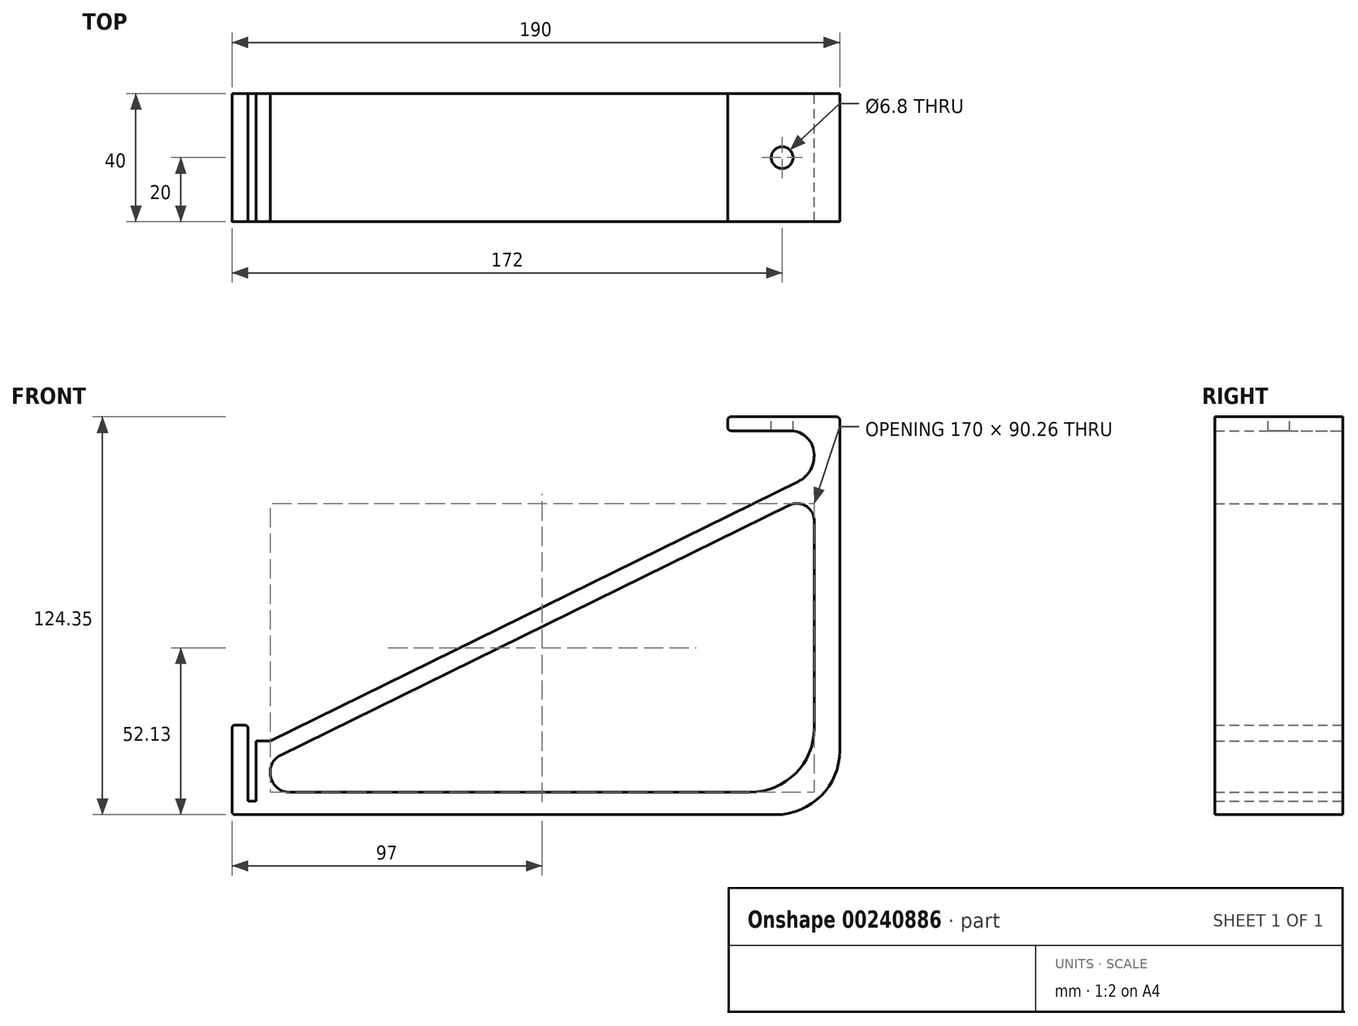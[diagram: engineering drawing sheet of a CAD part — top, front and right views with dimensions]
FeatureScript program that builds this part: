
annotation { "Feature Type Name" : "Feature", "Feature Type Description" : "" }
export const myFeature = defineFeature(function(context is Context, id is Id, definition is map)
    precondition{}
    {
        {
            var Q0;
            Q0=qCreatedBy(makeId("Front.planeOp"),FACE);
            var sketch = newSketch(context, id + "F0", { "sketchPlane" : qUnion([Q0])});
            skLineSegment(sketch, "E0", {"start": v(182, 27) * mm, "end": v(182, 91.87) * mm});
            skLineSegment(sketch, "E1", {"start": v(174.5, 120) * mm, "end": v(156, 120) * mm});
            skLineSegment(sketch, "E2", {"start": v(155, 121) * mm, "end": v(155, 123.35) * mm});
            skLineSegment(sketch, "E3", {"start": v(156, 124.35) * mm, "end": v(189, 124.35) * mm});
            skLineSegment(sketch, "E4", {"start": v(190, 123.35) * mm, "end": v(190, 120) * mm});
            skLineSegment(sketch, "E5", {"start": v(190, 120) * mm, "end": v(190, 120) * mm});
            skLineSegment(sketch, "E6", {"start": v(190, 120) * mm, "end": v(190, 20) * mm});
            skPoint(sketch, "E7", {"position": v(172, 154.35) * mm});
            skPoint(sketch, "E8", {"position": v(182, 124.35) * mm});
            skLineSegment(sketch, "E9", {"start": v(0, 1) * mm, "end": v(0, 27) * mm});
            skLineSegment(sketch, "E10", {"start": v(1, 28) * mm, "end": v(4, 28) * mm});
            skLineSegment(sketch, "E11", {"start": v(5, 27) * mm, "end": v(5, 4.2) * mm});
            skLineSegment(sketch, "E12", {"start": v(5, 4.2) * mm, "end": v(7.5, 4.2) * mm});
            skLineSegment(sketch, "E13", {"start": v(7.5, 4.2) * mm, "end": v(7.5, 23) * mm});
            skLineSegment(sketch, "E14", {"start": v(7.5, 23) * mm, "end": v(12, 23) * mm});
            skLineSegment(sketch, "E15", {"start": v(22, 7) * mm, "end": v(162, 7) * mm});
            skLineSegment(sketch, "E16", {"start": v(1, 0) * mm, "end": v(170, 0) * mm});
            skPoint(sketch, "E17.visualSharp", {"position": v(182, 7) * mm});
            skArc(sketch, "E17.filletArc", {"start": v(162, 7) * mm, "mid": v(176.14, 12.86) * mm, "end": v(182, 27) * mm});
            skPoint(sketch, "E18.visualSharp", {"position": v(182, 120) * mm});
            skArc(sketch, "E18.filletArc", {"start": v(182, 112.5) * mm, "mid": v(179.8, 117.8) * mm, "end": v(174.5, 120) * mm});
            skPoint(sketch, "E19.visualSharp", {"position": v(12, 7) * mm});
            skLineSegment(sketch, "E20", {"start": v(12, 23) * mm, "end": v(176.97, 104.08) * mm});
            skLineSegment(sketch, "E21", {"start": v(174.22, 96.71) * mm, "end": v(15.02, 18.47) * mm});
            skLineSegment(sketch, "E22", {"start": v(22, 7) * mm, "end": v(18, 7) * mm});
            skLineSegment(sketch, "E23", {"start": v(12, 13.62) * mm, "end": v(12, 13) * mm});
            skArc(sketch, "E24.filletArc", {"start": v(12, 13) * mm, "mid": v(13.76, 8.76) * mm, "end": v(18, 7) * mm});
            skPoint(sketch, "E25.visualSharp", {"position": v(12, 16.99) * mm});
            skArc(sketch, "E25.filletArc", {"start": v(15.02, 18.47) * mm, "mid": v(12.82, 16.48) * mm, "end": v(12, 13.62) * mm});
            skPoint(sketch, "E26.newPointA", {"position": v(182, 100.54) * mm});
            skArc(sketch, "E26.filletArc", {"start": v(182, 91.87) * mm, "mid": v(179.45, 96.45) * mm, "end": v(174.22, 96.71) * mm});
            skLineSegment(sketch, "E27", {"start": v(182, 112.15) * mm, "end": v(182, 112.5) * mm});
            skPoint(sketch, "E28.visualSharp", {"position": v(182, 106.55) * mm});
            skArc(sketch, "E28.filletArc", {"start": v(176.97, 104.08) * mm, "mid": v(180.64, 107.4) * mm, "end": v(182, 112.15) * mm});
            skPoint(sketch, "E29.visualSharp", {"position": v(0, 28) * mm});
            skArc(sketch, "E29.filletArc", {"start": v(1, 28) * mm, "mid": v(0.3, 27.7) * mm, "end": v(0, 27) * mm});
            skPoint(sketch, "E30.visualSharp", {"position": v(5, 28) * mm});
            skArc(sketch, "E30.filletArc", {"start": v(5, 27) * mm, "mid": v(4.7, 27.7) * mm, "end": v(4, 28) * mm});
            skPoint(sketch, "E31.visualSharp", {"position": v(0, 0) * mm});
            skArc(sketch, "E31.filletArc", {"start": v(0, 1) * mm, "mid": v(0.3, 0.3) * mm, "end": v(1, 0) * mm});
            skPoint(sketch, "E32.visualSharp", {"position": v(190, 0) * mm});
            skArc(sketch, "E32.filletArc", {"start": v(170, 0) * mm, "mid": v(184.14, 5.86) * mm, "end": v(190, 20) * mm});
            skPoint(sketch, "E33.visualSharp", {"position": v(190, 124.35) * mm});
            skArc(sketch, "E33.filletArc", {"start": v(190, 123.35) * mm, "mid": v(189.7, 124.06) * mm, "end": v(189, 124.35) * mm});
            skPoint(sketch, "E34.visualSharp", {"position": v(155, 124.35) * mm});
            skArc(sketch, "E34.filletArc", {"start": v(156, 124.35) * mm, "mid": v(155.3, 124.06) * mm, "end": v(155, 123.35) * mm});
            skPoint(sketch, "E35.visualSharp", {"position": v(155, 120) * mm});
            skArc(sketch, "E35.filletArc", {"start": v(155, 121) * mm, "mid": v(155.3, 120.3) * mm, "end": v(156, 120) * mm});
            skSolve(sketch);
        }
        {
            var Q0;
            Q0 = qSketchRegion(id + "F0", true);
            extrude(context, id + "F1", {"entities" : qUnion([Q0]), "endBound" : BoundingType.SYMMETRIC, "depth" : 40 * mm});
        }
        {
            var Q0;
            Q0=qCreatedBy(makeId("Top.planeOp"),FACE);
            cPlane(context, id + "F2", {"entities" : qUnion([Q0]), "cplaneType" : CPlaneType.OFFSET, "offset" : 125 * mm, "width" : 150 * mm, "height" : 150 * mm});
        }
        {
            var Q0;
            Q0=qCreatedBy(id+"F2.planeOp",FACE);
            var sketch = newSketch(context, id + "F3", { "sketchPlane" : qUnion([Q0])});
            skPoint(sketch, "E36.0", {"position": v(172, 0) * mm});
            skLineSegment(sketch, "E37.0.0", {"start": v(156, 20) * mm, "end": v(156, 20) * mm});
            skLineSegment(sketch, "E37.0.1", {"start": v(156, 20) * mm, "end": v(156, -20) * mm});
            skLineSegment(sketch, "E37.0.2", {"start": v(156, -20) * mm, "end": v(156, -20) * mm});
            skLineSegment(sketch, "E37.0.3", {"start": v(156, -20) * mm, "end": v(156, 20) * mm});
            skPoint(sketch, "E38.0", {"position": v(172.5, 0) * mm});
            skCircle(sketch, "E39", {"center": v(172, 0) * mm, "radius": 3.4 * mm});
            skCircle(sketch, "E40", {"center": v(172, 0) * mm, "radius": 10 * mm, "construction": true});
            skPoint(sketch, "E41.0", {"position": v(81.5, 0) * mm});
            skSolve(sketch);
        }
        {
            var Q0;
            Q0=makeQuery(id+"F3.imprint","IMPRINT",FACE,{"disambiguationData":[TD([[makeQuery(id+"F3.imprint","IMPRINT",EDGE,{"derivedFrom":sQuery(id+"F3.wireOp",EDGE,"E39")}),1.0]])]});
            extrude(context, id + "F4", {"entities" : qUnion([Q0]), "operationType" : NewBodyOperationType.REMOVE, "oppositeDirection" : true, "offsetDistance" : 25 * mm, "depth" : 10 * mm});
        }
    });
